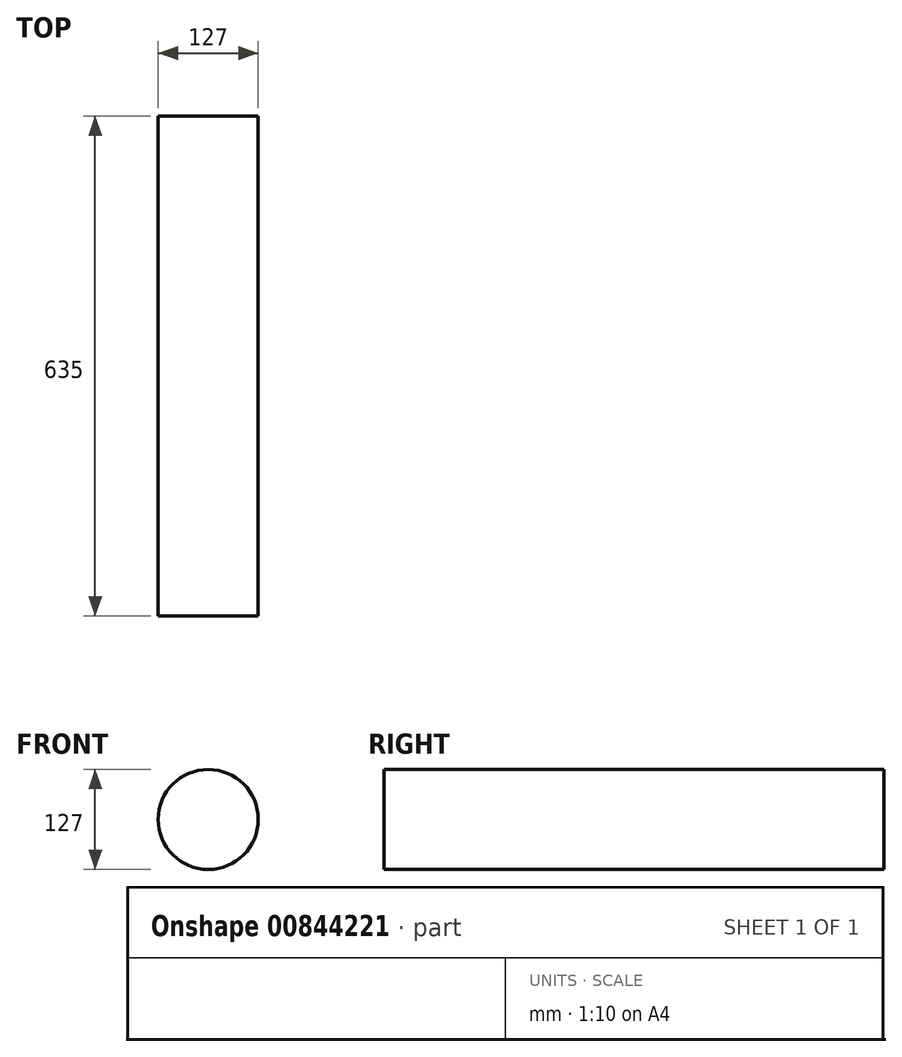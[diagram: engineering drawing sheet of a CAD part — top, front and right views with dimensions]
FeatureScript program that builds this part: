
annotation { "Feature Type Name" : "Feature", "Feature Type Description" : "" }
export const myFeature = defineFeature(function(context is Context, id is Id, definition is map)
    precondition{}
    {
        {
            var Q0;
            Q0=qCreatedBy(makeId("Front.planeOp"),FACE);
            var sketch = newSketch(context, id + "F0", { "sketchPlane" : qUnion([Q0])});
            skCircle(sketch, "E0", {"center": v(0, 0) * mm, "radius": 63.5 * mm});
            skSolve(sketch);
        }
        {
            var Q0;
            Q0 = qSketchRegion(id + "F0", true);
            extrude(context, id + "F1", {"entities" : qUnion([Q0]), "depth" : 635 * mm, "offsetDistance" : 25.4 * mm});
        }
    });
